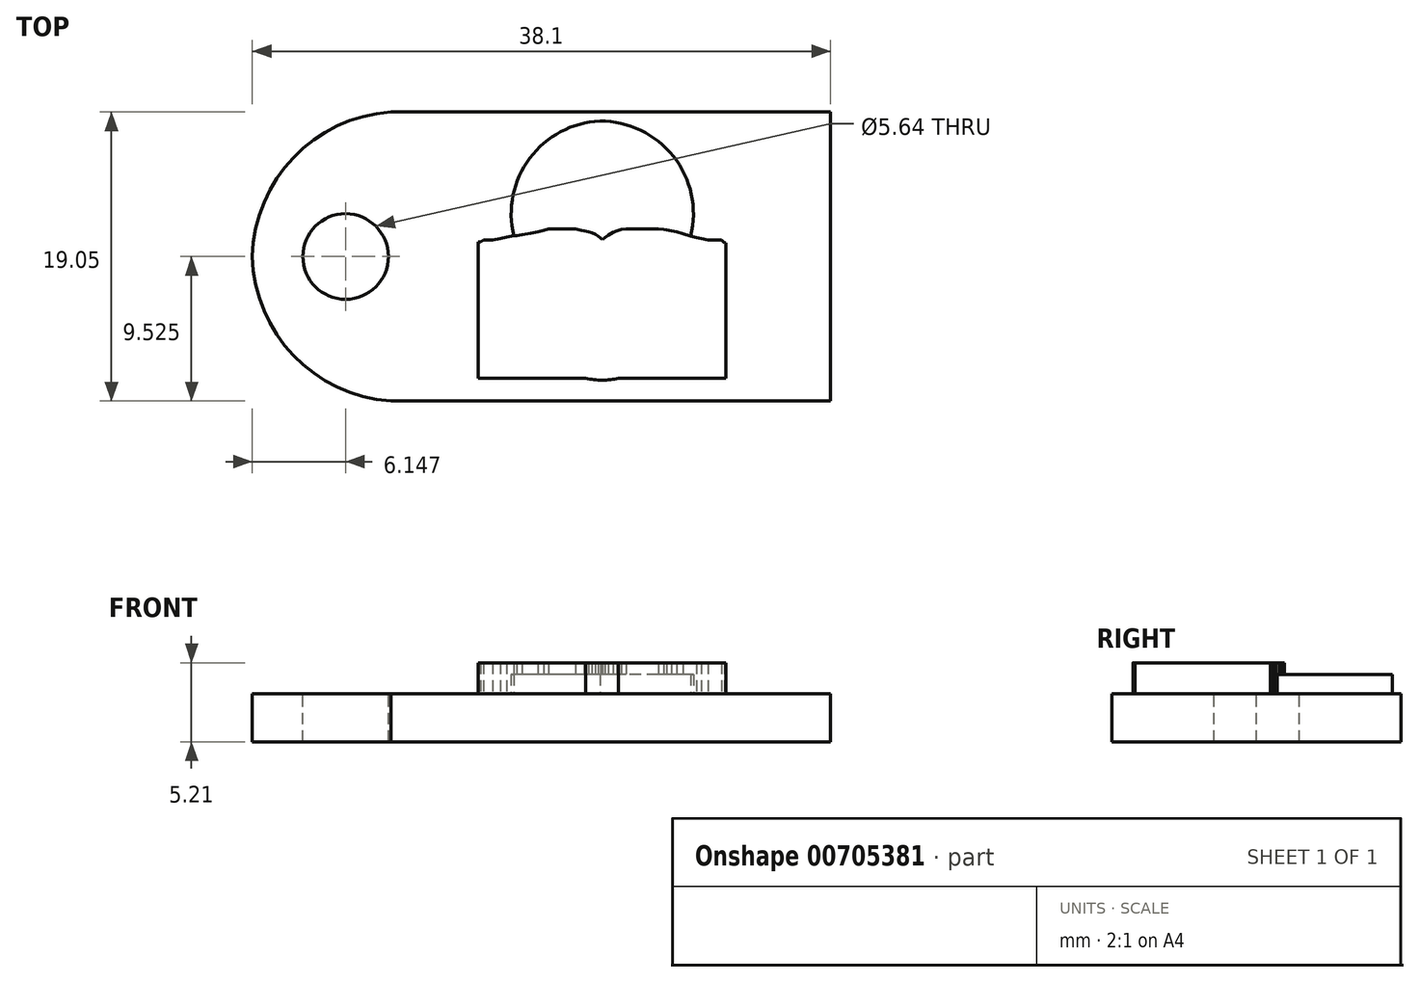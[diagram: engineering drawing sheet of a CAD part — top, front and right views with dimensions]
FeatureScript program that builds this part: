
annotation { "Feature Type Name" : "Feature", "Feature Type Description" : "" }
export const myFeature = defineFeature(function(context is Context, id is Id, definition is map)
    precondition{}
    {
        {
            var Q0;
            Q0=qCreatedBy(makeId("Top.planeOp"),FACE);
            var sketch = newSketch(context, id + "F0", { "sketchPlane" : qUnion([Q0])});
            skLineSegment(sketch, "E0.bottom", {"start": v(0, 0) * mm, "end": v(-38.1, 0) * mm});
            skLineSegment(sketch, "E0.top", {"start": v(0, 19.05) * mm, "end": v(-38.1, 19.05) * mm});
            skLineSegment(sketch, "E0.left", {"start": v(0, 0) * mm, "end": v(0, 19.05) * mm});
            skLineSegment(sketch, "E0.right", {"start": v(-38.1, 0) * mm, "end": v(-38.1, 19.05) * mm});
            skSolve(sketch);
        }
        {
            var Q0;
            Q0 = qSketchRegion(id + "F0", true);
            extrude(context, id + "F1", {"entities" : qUnion([Q0]), "depth" : 3.17 * mm, "offsetDistance" : 25.4 * mm});
        }
        {
            var Q0;
            Q0=makeQuery(id+"F1.opExtrude","CAP_FACE",FACE,{"disambiguationData":[OSD([sQuery(id+"F0.wireOp",EDGE,"E0.bottom"),sQuery(id+"F0.wireOp",EDGE,"E0.top"),sQuery(id+"F0.wireOp",EDGE,"E0.left"),sQuery(id+"F0.wireOp",EDGE,"E0.right")])],"isStart":false});
            var sketch = newSketch(context, id + "F2", { "sketchPlane" : qUnion([Q0])});
            skLineSegment(sketch, "E1", {"start": v(-38.1, 9.52) * mm, "end": v(0, 9.53) * mm, "construction": true});
            skArc(sketch, "E2", {"start": v(-27.64, 19.05) * mm, "mid": v(-34.9, 16.52) * mm, "end": v(-38.1, 9.52) * mm});
            skArc(sketch, "E3.MirrorCS", {"start": v(-27.64, 0) * mm, "mid": v(-34.9, 2.53) * mm, "end": v(-38.1, 9.53) * mm});
            skCircle(sketch, "E4", {"center": v(-31.95, 9.52) * mm, "radius": 2.82 * mm});
            skSolve(sketch);
        }
        {
            var Q0;
            {var subQ1=makeQuery(id+"F1.opExtrude","CAP_EDGE",EDGE,{"disambiguationData":[OSD([sQuery(id+"F0.wireOp",EDGE,"E0.right")])],"isStart":false});var subQ3=makeQuery(id+"F1.opExtrude","CAP_EDGE",EDGE,{"disambiguationData":[OSD([sQuery(id+"F0.wireOp",EDGE,"E0.top")])],"isStart":false});var subQ5=makeQuery(id+"F2.imprint","INTERSECT",VERTEX,{"derivedFrom":[subQ3,subQ1]});Q0=makeQuery(id+"F2.imprint","IMPRINT",FACE,{"disambiguationData":[TD([[makeQuery(id+"F2.imprint","IMPRINT",EDGE,{"disambiguationData":[TD([[subQ5,1.0]])],"derivedFrom":subQ3}),1.0]])]});}
            var Q1;
            {var subQ1=makeQuery(id+"F1.opExtrude","CAP_EDGE",EDGE,{"disambiguationData":[OSD([sQuery(id+"F0.wireOp",EDGE,"E0.right")])],"isStart":false});var subQ3=makeQuery(id+"F1.opExtrude","CAP_EDGE",EDGE,{"disambiguationData":[OSD([sQuery(id+"F0.wireOp",EDGE,"E0.bottom")])],"isStart":false});var subQ5=makeQuery(id+"F2.imprint","INTERSECT",VERTEX,{"derivedFrom":[subQ3,subQ1]});Q1=makeQuery(id+"F2.imprint","IMPRINT",FACE,{"disambiguationData":[TD([[makeQuery(id+"F2.imprint","IMPRINT",EDGE,{"disambiguationData":[TD([[subQ5,1.0]])],"derivedFrom":subQ3}),-1.0]])]});}
            var Q2;
            Q2=makeQuery(id+"F2.imprint","IMPRINT",FACE,{"disambiguationData":[TD([[makeQuery(id+"F2.imprint","IMPRINT",EDGE,{"derivedFrom":sQuery(id+"F2.wireOp",EDGE,"E4")}),1.0]])]});
            extrude(context, id + "F3", {"entities" : qUnion([Q0, Q1, Q2]), "operationType" : NewBodyOperationType.REMOVE, "endBound" : BoundingType.THROUGH_ALL, "oppositeDirection" : true, "depth" : 25.4 * mm, "offsetDistance" : 25.4 * mm});
        }
        {
            var Q0;
            Q0=makeQuery(id+"F1.opExtrude","CAP_FACE",FACE,{"disambiguationData":[OSD([sQuery(id+"F0.wireOp",EDGE,"E0.bottom"),sQuery(id+"F0.wireOp",EDGE,"E0.top"),sQuery(id+"F0.wireOp",EDGE,"E0.left"),sQuery(id+"F0.wireOp",EDGE,"E0.right")])],"isStart":false});
            var sketch = newSketch(context, id + "F4", { "sketchPlane" : qUnion([Q0])});
            skLineSegment(sketch, "E5", {"start": v(-23.23, 10.5) * mm, "end": v(-23.07, 10.5) * mm});
            skLineSegment(sketch, "E6", {"start": v(-23.07, 10.5) * mm, "end": v(-22.87, 10.61) * mm});
            skLineSegment(sketch, "E7", {"start": v(-22.87, 10.61) * mm, "end": v(-22.28, 10.61) * mm});
            skLineSegment(sketch, "E8", {"start": v(-22.28, 10.61) * mm, "end": v(-21.75, 10.7) * mm});
            skLineSegment(sketch, "E9", {"start": v(-21.75, 10.7) * mm, "end": v(-21.35, 10.8) * mm});
            skLineSegment(sketch, "E10", {"start": v(-21.35, 10.8) * mm, "end": v(-20.87, 10.88) * mm});
            skLineSegment(sketch, "E11", {"start": v(-23.23, 10.5) * mm, "end": v(-23.23, 1.51) * mm});
            skLineSegment(sketch, "E12", {"start": v(-23.23, 1.51) * mm, "end": v(-16.13, 1.51) * mm});
            skArc(sketch, "E13", {"start": v(-16.13, 1.51) * mm, "mid": v(-15.05, 1.37) * mm, "end": v(-13.96, 1.51) * mm});
            skLineSegment(sketch, "E14", {"start": v(-13.96, 1.51) * mm, "end": v(-6.89, 1.51) * mm});
            skLineSegment(sketch, "E15", {"start": v(-6.89, 1.51) * mm, "end": v(-6.89, 10.44) * mm});
            skLineSegment(sketch, "E16", {"start": v(-6.89, 10.44) * mm, "end": v(-7, 10.44) * mm});
            skLineSegment(sketch, "E17", {"start": v(-7, 10.44) * mm, "end": v(-7.2, 10.62) * mm});
            skLineSegment(sketch, "E18", {"start": v(-7.2, 10.62) * mm, "end": v(-7.65, 10.62) * mm});
            skLineSegment(sketch, "E19", {"start": v(-7.65, 10.62) * mm, "end": v(-8.06, 10.62) * mm});
            skLineSegment(sketch, "E20", {"start": v(-8.06, 10.62) * mm, "end": v(-8.5, 10.7) * mm});
            skLineSegment(sketch, "E21", {"start": v(-8.5, 10.7) * mm, "end": v(-8.85, 10.78) * mm});
            skLineSegment(sketch, "E22", {"start": v(-8.85, 10.78) * mm, "end": v(-9.21, 10.88) * mm});
            skLineSegment(sketch, "E23", {"start": v(-9.21, 10.88) * mm, "end": v(-9.73, 11.03) * mm});
            skLineSegment(sketch, "E24", {"start": v(-9.73, 11.03) * mm, "end": v(-10.13, 11.14) * mm});
            skLineSegment(sketch, "E25", {"start": v(-10.13, 11.14) * mm, "end": v(-10.47, 11.22) * mm});
            skLineSegment(sketch, "E26", {"start": v(-10.47, 11.22) * mm, "end": v(-10.8, 11.26) * mm});
            skLineSegment(sketch, "E27", {"start": v(-10.8, 11.26) * mm, "end": v(-10.99, 11.3) * mm});
            skLineSegment(sketch, "E28", {"start": v(-10.99, 11.3) * mm, "end": v(-11.36, 11.35) * mm});
            skLineSegment(sketch, "E29", {"start": v(-11.36, 11.35) * mm, "end": v(-11.75, 11.35) * mm});
            skLineSegment(sketch, "E30", {"start": v(-11.75, 11.35) * mm, "end": v(-12.15, 11.35) * mm});
            skLineSegment(sketch, "E31", {"start": v(-12.15, 11.35) * mm, "end": v(-12.55, 11.35) * mm});
            skLineSegment(sketch, "E32", {"start": v(-12.55, 11.35) * mm, "end": v(-12.89, 11.35) * mm});
            skLineSegment(sketch, "E33", {"start": v(-12.89, 11.35) * mm, "end": v(-13.24, 11.35) * mm});
            skLineSegment(sketch, "E34", {"start": v(-13.24, 11.35) * mm, "end": v(-13.48, 11.35) * mm});
            skLineSegment(sketch, "E35", {"start": v(-13.48, 11.35) * mm, "end": v(-13.78, 11.3) * mm});
            skLineSegment(sketch, "E36", {"start": v(-13.78, 11.3) * mm, "end": v(-14.08, 11.22) * mm});
            skLineSegment(sketch, "E37", {"start": v(-14.08, 11.22) * mm, "end": v(-14.32, 11.11) * mm});
            skLineSegment(sketch, "E38", {"start": v(-14.32, 11.11) * mm, "end": v(-14.65, 10.92) * mm});
            skLineSegment(sketch, "E39", {"start": v(-14.65, 10.92) * mm, "end": v(-14.87, 10.76) * mm});
            skLineSegment(sketch, "E40", {"start": v(-14.87, 10.76) * mm, "end": v(-15.02, 10.64) * mm});
            skLineSegment(sketch, "E41", {"start": v(-15.02, 10.64) * mm, "end": v(-15.15, 10.74) * mm});
            skLineSegment(sketch, "E42", {"start": v(-15.15, 10.74) * mm, "end": v(-15.33, 10.87) * mm});
            skLineSegment(sketch, "E43", {"start": v(-15.33, 10.87) * mm, "end": v(-15.5, 10.98) * mm});
            skLineSegment(sketch, "E44", {"start": v(-15.5, 10.98) * mm, "end": v(-15.72, 11.09) * mm});
            skLineSegment(sketch, "E45", {"start": v(-15.72, 11.09) * mm, "end": v(-15.96, 11.16) * mm});
            skLineSegment(sketch, "E46", {"start": v(-15.96, 11.16) * mm, "end": v(-16.23, 11.23) * mm});
            skLineSegment(sketch, "E47", {"start": v(-16.23, 11.23) * mm, "end": v(-16.43, 11.26) * mm});
            skLineSegment(sketch, "E48", {"start": v(-16.43, 11.26) * mm, "end": v(-16.8, 11.33) * mm});
            skLineSegment(sketch, "E49", {"start": v(-16.8, 11.33) * mm, "end": v(-17.22, 11.33) * mm});
            skLineSegment(sketch, "E50", {"start": v(-17.22, 11.33) * mm, "end": v(-17.76, 11.33) * mm});
            skLineSegment(sketch, "E51", {"start": v(-17.76, 11.33) * mm, "end": v(-18.26, 11.33) * mm});
            skLineSegment(sketch, "E52", {"start": v(-18.26, 11.33) * mm, "end": v(-18.59, 11.33) * mm});
            skLineSegment(sketch, "E53", {"start": v(-18.59, 11.33) * mm, "end": v(-18.91, 11.26) * mm});
            skLineSegment(sketch, "E54", {"start": v(-18.91, 11.26) * mm, "end": v(-19.3, 11.16) * mm});
            skLineSegment(sketch, "E55", {"start": v(-19.3, 11.16) * mm, "end": v(-19.77, 11.07) * mm});
            skLineSegment(sketch, "E56", {"start": v(-19.77, 11.07) * mm, "end": v(-20.32, 10.96) * mm});
            skLineSegment(sketch, "E57", {"start": v(-20.32, 10.96) * mm, "end": v(-20.67, 10.88) * mm});
            skLineSegment(sketch, "E58", {"start": v(-20.67, 10.88) * mm, "end": v(-20.87, 10.88) * mm});
            skArc(sketch, "E59", {"start": v(-15.2, 18.45) * mm, "mid": v(-19.82, 16) * mm, "end": v(-20.87, 10.88) * mm});
            skArc(sketch, "E60", {"start": v(-9.21, 10.88) * mm, "mid": v(-10.36, 16.12) * mm, "end": v(-15.2, 18.45) * mm});
            skSolve(sketch);
        }
        {
            var Q0;
            Q0=makeQuery(id+"F4.imprint","IMPRINT",FACE,{"disambiguationData":[TD([[makeQuery(id+"F4.imprint","IMPRINT",EDGE,{"derivedFrom":sQuery(id+"F4.wireOp",EDGE,"E23")}),-1.0]])]});
            extrude(context, id + "F5", {"entities" : qUnion([Q0]), "operationType" : NewBodyOperationType.ADD, "depth" : 1.27 * mm, "offsetDistance" : 25.4 * mm});
        }
        {
            var Q0;
            Q0=makeQuery(id+"F4.imprint","IMPRINT",FACE,{"disambiguationData":[TD([[makeQuery(id+"F4.imprint","IMPRINT",EDGE,{"derivedFrom":sQuery(id+"F4.wireOp",EDGE,"E5")}),-1.0]])]});
            extrude(context, id + "F6", {"entities" : qUnion([Q0]), "operationType" : NewBodyOperationType.ADD, "depth" : 2.03 * mm, "offsetDistance" : 25.4 * mm});
        }
    });
